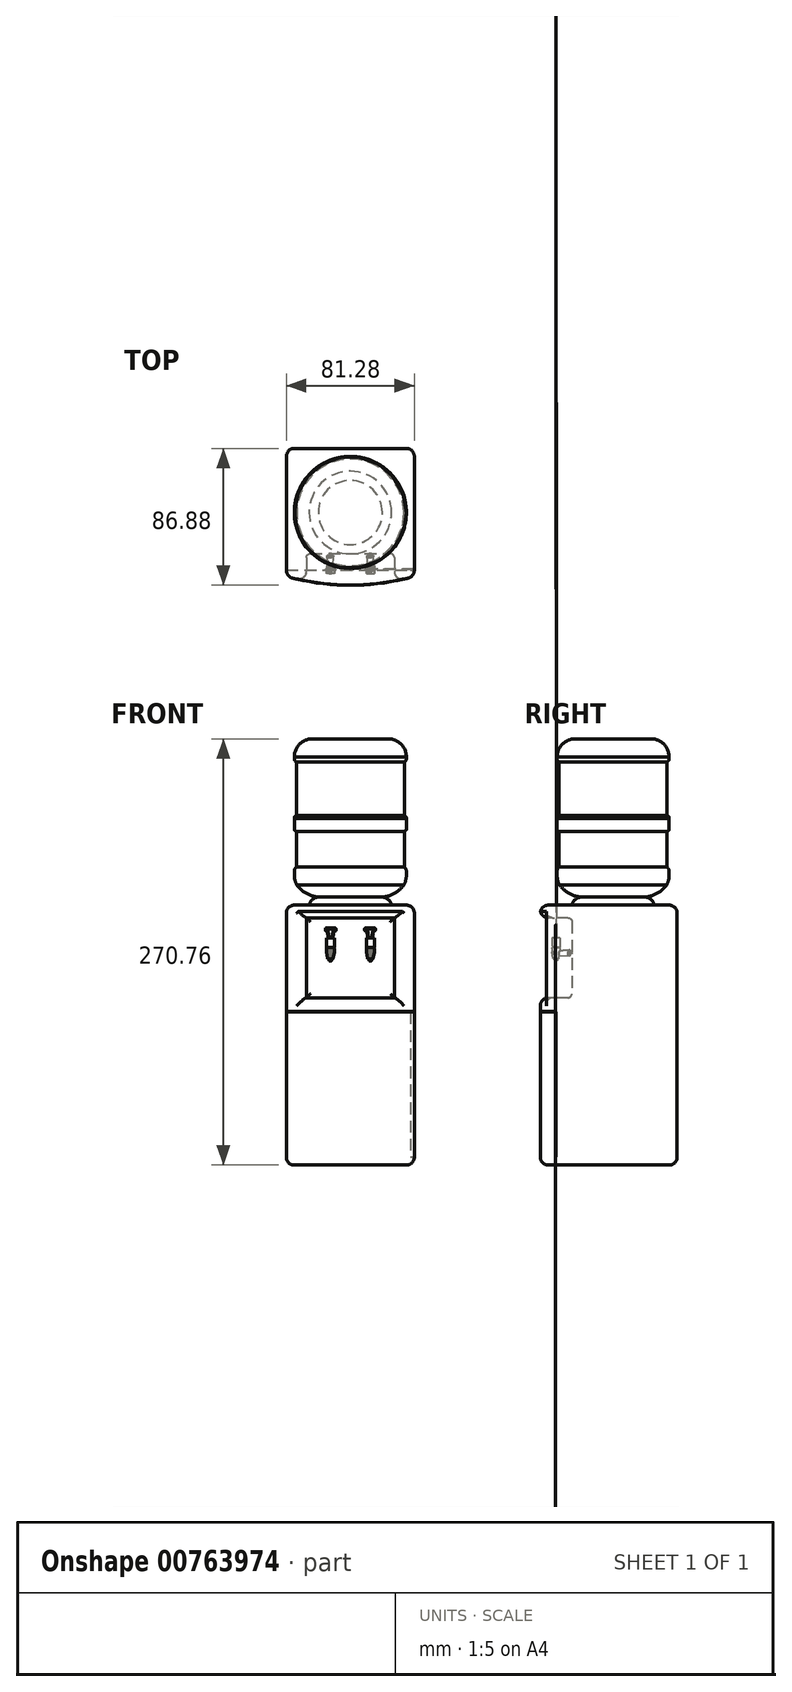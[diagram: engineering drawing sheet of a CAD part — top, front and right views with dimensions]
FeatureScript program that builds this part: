
annotation { "Feature Type Name" : "Feature", "Feature Type Description" : "" }
export const myFeature = defineFeature(function(context is Context, id is Id, definition is map)
    precondition{}
    {
        {
            var Q0;
            Q0=qCreatedBy(makeId("Front.planeOp"),FACE);
            var sketch = newSketch(context, id + "F0", { "sketchPlane" : qUnion([Q0])});
            skLineSegment(sketch, "E0", {"start": v(0, 95.92) * mm, "end": v(24.1, 95.92) * mm});
            skLineSegment(sketch, "E1", {"start": v(0, 11.85) * mm, "end": v(35.56, 11.85) * mm, "construction": true});
            skLineSegment(sketch, "E2", {"start": v(0, 83.22) * mm, "end": v(35.56, 83.22) * mm, "construction": true});
            skLineSegment(sketch, "E3", {"start": v(0, 81.19) * mm, "end": v(34.29, 81.11) * mm, "construction": true});
            skPoint(sketch, "E4.visualSharp", {"position": v(35.56, 95.92) * mm});
            skArc(sketch, "E4.filletArc", {"start": v(35.53, 84.46) * mm, "mid": v(32.2, 92.56) * mm, "end": v(24.1, 95.92) * mm});
            skLineSegment(sketch, "E5", {"start": v(35.53, 84.46) * mm, "end": v(35.56, 83.22) * mm});
            skLineSegment(sketch, "E6", {"start": v(0, 47.4) * mm, "end": v(38.08, 47.32) * mm, "construction": true});
            skLineSegment(sketch, "E7", {"start": v(34.29, 81.11) * mm, "end": v(34.29, 47.33) * mm});
            skLineSegment(sketch, "E8", {"start": v(0, 45.37) * mm, "end": v(35.56, 45.37) * mm, "construction": true});
            skLineSegment(sketch, "E9", {"start": v(0, 38.52) * mm, "end": v(35.56, 38.44) * mm, "construction": true});
            skLineSegment(sketch, "E10", {"start": v(0, 37.25) * mm, "end": v(34.29, 37.17) * mm, "construction": true});
            skArc(sketch, "E11", {"start": v(35.56, 83.22) * mm, "mid": v(35.23, 81.98) * mm, "end": v(34.29, 81.11) * mm});
            skArc(sketch, "E12", {"start": v(35.56, 45.37) * mm, "mid": v(35.23, 46.55) * mm, "end": v(34.29, 47.33) * mm});
            skArc(sketch, "E13", {"start": v(34.29, 37.17) * mm, "mid": v(35.19, 37.54) * mm, "end": v(35.56, 38.44) * mm});
            skLineSegment(sketch, "E14", {"start": v(35.56, 45.37) * mm, "end": v(35.56, 38.44) * mm});
            skLineSegment(sketch, "E15", {"start": v(0, 14.39) * mm, "end": v(34.3, 14.39) * mm, "construction": true});
            skLineSegment(sketch, "E16", {"start": v(0, 2.96) * mm, "end": v(33.95, 2.96) * mm, "construction": true});
            skLineSegment(sketch, "E17", {"start": v(34.29, 37.17) * mm, "end": v(34.3, 14.39) * mm});
            skLineSegment(sketch, "E18", {"start": v(0, -4.66) * mm, "end": v(20.35, -4.66) * mm, "construction": true});
            skLineSegment(sketch, "E19", {"start": v(0, -9.74) * mm, "end": v(26.2, -9.74) * mm});
            skArc(sketch, "E20", {"start": v(35.56, 11.85) * mm, "mid": v(35.22, 13.27) * mm, "end": v(34.3, 14.39) * mm});
            skLineSegment(sketch, "E21", {"start": v(35.56, 11.85) * mm, "end": v(35.57, 9.23) * mm});
            skArc(sketch, "E22", {"start": v(33.95, 2.96) * mm, "mid": v(35.16, 5.99) * mm, "end": v(35.57, 9.23) * mm});
            skArc(sketch, "E23", {"start": v(20.35, -4.66) * mm, "mid": v(27.95, -2.29) * mm, "end": v(33.95, 2.96) * mm});
            skArc(sketch, "E24", {"start": v(26.2, -9.74) * mm, "mid": v(24.13, -6.22) * mm, "end": v(20.35, -4.66) * mm});
            skLineSegment(sketch, "E25", {"start": v(0, 95.92) * mm, "end": v(0, -9.74) * mm});
            skSolve(sketch);
        }
        {
            var Q0;
            Q0 = qSketchRegion(id + "F0", true);
            var Q1;
            Q1=sQuery(id+"F0.wireOp",EDGE,"E25");
            revolve(context, id + "F1", {"surfaceOperationType" : NewSurfaceOperationType.NEW, "entities" : qUnion([Q0]), "axis" : qUnion([Q1]), "revolveType" : RevolveType.FULL});
        }
        {
            var Q0;
            Q0=makeQuery(id+"F1.opRevolve","SWEPT_FACE",FACE,{"disambiguationData":[OSD([sQuery(id+"F0.wireOp",EDGE,"E19")])]});
            cPlane(context, id + "F2", {"entities" : qUnion([Q0]), "cplaneType" : CPlaneType.OFFSET, "offset" : 0 * mm, "width" : 152.4 * mm, "height" : 152.4 * mm});
        }
        {
            var Q0;
            Q0=qCreatedBy(id+"F2.planeOp",FACE);
            var sketch = newSketch(context, id + "F3", { "sketchPlane" : qUnion([Q0])});
            skLineSegment(sketch, "E26.top", {"start": v(-40.64, -40.64) * mm, "end": v(40.64, -40.64) * mm});
            skLineSegment(sketch, "E26.left", {"start": v(-40.64, 40.64) * mm, "end": v(-40.64, -40.64) * mm});
            skLineSegment(sketch, "E26.right", {"start": v(40.64, 40.64) * mm, "end": v(40.64, -40.64) * mm});
            skArc(sketch, "E27", {"start": v(40.64, 40.64) * mm, "mid": v(0, 46.24) * mm, "end": v(-40.64, 40.64) * mm});
            skSolve(sketch);
        }
        {
            var Q0;
            Q0 = qSketchRegion(id + "F3", true);
            extrude(context, id + "F4", {"entities" : qUnion([Q0]), "operationType" : NewBodyOperationType.ADD, "depth" : 165.1 * mm, "offsetDistance" : 25.4 * mm});
        }
        {
            var Q0;
            Q0=qCreatedBy(makeId("Front.planeOp"),FACE);
            cPlane(context, id + "F5", {"entities" : qUnion([Q0]), "cplaneType" : CPlaneType.OFFSET, "offset" : 46.48 * mm, "width" : 152.4 * mm, "height" : 152.4 * mm});
        }
        {
            var Q0;
            Q0=qCreatedBy(id+"F5.planeOp",FACE);
            var sketch = newSketch(context, id + "F6", { "sketchPlane" : qUnion([Q0])});
            skLineSegment(sketch, "E28.bottom", {"start": v(-27.94, -17.78) * mm, "end": v(27.94, -17.78) * mm});
            skLineSegment(sketch, "E28.top", {"start": v(-27.94, -68.58) * mm, "end": v(27.94, -68.58) * mm});
            skLineSegment(sketch, "E28.left", {"start": v(-27.94, -17.78) * mm, "end": v(-27.94, -68.58) * mm});
            skLineSegment(sketch, "E28.right", {"start": v(27.94, -17.78) * mm, "end": v(27.94, -68.58) * mm});
            skSolve(sketch);
        }
        {
            var Q0;
            Q0 = qSketchRegion(id + "F6", true);
            extrude(context, id + "F7", {"entities" : qUnion([Q0]), "operationType" : NewBodyOperationType.REMOVE, "oppositeDirection" : true, "depth" : 20.32 * mm, "offsetDistance" : 25.4 * mm});
        }
        {
            var Q0;
            Q0=makeQuery(id+"F4.opExtrude","CAP_EDGE",EDGE,{"disambiguationData":[OSD([sQuery(id+"F3.wireOp",EDGE,"E26.left")])],"isStart":true});
            var Q1;
            Q1=makeQuery(id+"F4.opExtrude","SWEPT_EDGE",EDGE,{"disambiguationData":[OSD([sQuery(id+"F3.wireOp",EDGE,"E26.top"),sQuery(id+"F3.wireOp",EDGE,"E26.left")])]});
            var Q2;
            Q2=makeQuery(id+"F4.opExtrude","SWEPT_EDGE",EDGE,{"disambiguationData":[OSD([sQuery(id+"F3.wireOp",EDGE,"E26.left"),sQuery(id+"F3.wireOp",EDGE,"E27")])]});
            var Q3;
            Q3=makeQuery(id+"F4.opExtrude","CAP_EDGE",EDGE,{"disambiguationData":[OSD([sQuery(id+"F3.wireOp",EDGE,"E27")])],"isStart":true});
            var Q4;
            Q4=makeQuery(id+"F4.opExtrude","SWEPT_EDGE",EDGE,{"disambiguationData":[OSD([sQuery(id+"F3.wireOp",EDGE,"E26.right"),sQuery(id+"F3.wireOp",EDGE,"E27")])]});
            var Q5;
            Q5=makeQuery(id+"F4.opExtrude","CAP_EDGE",EDGE,{"disambiguationData":[OSD([sQuery(id+"F3.wireOp",EDGE,"E26.right")])],"isStart":true});
            var Q6;
            Q6=makeQuery(id+"F4.opExtrude","SWEPT_EDGE",EDGE,{"disambiguationData":[OSD([sQuery(id+"F3.wireOp",EDGE,"E26.top"),sQuery(id+"F3.wireOp",EDGE,"E26.right")])]});
            var Q7;
            Q7=makeQuery(id+"F4.opExtrude","CAP_EDGE",EDGE,{"disambiguationData":[OSD([sQuery(id+"F3.wireOp",EDGE,"E26.right")])],"isStart":false});
            var Q8;
            Q8=makeQuery(id+"F4.opExtrude","CAP_EDGE",EDGE,{"disambiguationData":[OSD([sQuery(id+"F3.wireOp",EDGE,"E27")])],"isStart":false});
            var Q9;
            Q9=makeQuery(id+"F4.opExtrude","CAP_EDGE",EDGE,{"disambiguationData":[OSD([sQuery(id+"F3.wireOp",EDGE,"E26.left")])],"isStart":false});
            var Q10;
            Q10=makeQuery(id+"F4.opExtrude","CAP_EDGE",EDGE,{"disambiguationData":[OSD([sQuery(id+"F3.wireOp",EDGE,"E26.top")])],"isStart":true});
            var Q11;
            Q11=makeQuery(id+"F4.opExtrude","CAP_EDGE",EDGE,{"disambiguationData":[OSD([sQuery(id+"F3.wireOp",EDGE,"E26.top")])],"isStart":false});
            fillet(context, id + "F8", {"entities" : qUnion([Q0, Q1, Q2, Q3, Q4, Q5, Q6, Q7, Q8, Q9, Q10, Q11]), "radius" : 5.08 * mm, "tangentPropagation" : true, "allowEdgeOverflow" : false});
        }
        {
            var Q0;
            Q0=qCreatedBy(id+"F5.planeOp",FACE);
            var sketch = newSketch(context, id + "F9", { "sketchPlane" : qUnion([Q0])});
            skLineSegment(sketch, "E29.bottom", {"start": v(-49.64, -77.18) * mm, "end": v(53.25, -77.18) * mm});
            skLineSegment(sketch, "E29.top", {"start": v(-49.64, -77.69) * mm, "end": v(53.25, -77.69) * mm});
            skLineSegment(sketch, "E29.left", {"start": v(-49.64, -77.18) * mm, "end": v(-49.64, -77.69) * mm});
            skLineSegment(sketch, "E29.right", {"start": v(53.25, -77.18) * mm, "end": v(53.25, -77.69) * mm});
            skSolve(sketch);
        }
        {
            var Q0;
            Q0 = qSketchRegion(id + "F9", true);
            extrude(context, id + "F10", {"entities" : qUnion([Q0]), "operationType" : NewBodyOperationType.REMOVE, "oppositeDirection" : true, "depth" : 9.9 * mm, "offsetDistance" : 25.4 * mm});
        }
        {
            var Q0;
            Q0=makeQuery(id+"F7.boolean.opBoolean","COPY",FACE,{"derivedFrom":makeQuery(id+"F7.opExtrude","CAP_FACE",FACE,{"disambiguationData":[OSD([sQuery(id+"F6.wireOp",EDGE,"E28.bottom"),sQuery(id+"F6.wireOp",EDGE,"E28.top"),sQuery(id+"F6.wireOp",EDGE,"E28.left"),sQuery(id+"F6.wireOp",EDGE,"E28.right")])],"isStart":false})});
            fillet(context, id + "F11", {"entities" : qUnion([Q0]), "radius" : 2.54 * mm, "tangentPropagation" : true, "allowEdgeOverflow" : false});
        }
        {
            var Q0;
            Q0=makeQuery(id+"F7.boolean.opBoolean","INTERSECT",EDGE,{"derivedFrom":[makeQuery(id+"F4.opExtrude","SWEPT_FACE",FACE,{"disambiguationData":[OSD([sQuery(id+"F3.wireOp",EDGE,"E27")])]}),makeQuery(id+"F7.opExtrude","SWEPT_FACE",FACE,{"disambiguationData":[OSD([sQuery(id+"F6.wireOp",EDGE,"E28.bottom")])]})]});
            var Q1;
            Q1=makeQuery(id+"F7.boolean.opBoolean","INTERSECT",EDGE,{"derivedFrom":[makeQuery(id+"F4.opExtrude","SWEPT_FACE",FACE,{"disambiguationData":[OSD([sQuery(id+"F3.wireOp",EDGE,"E27")])]}),makeQuery(id+"F7.opExtrude","SWEPT_FACE",FACE,{"disambiguationData":[OSD([sQuery(id+"F6.wireOp",EDGE,"E28.right")])]})]});
            var Q2;
            Q2=makeQuery(id+"F7.boolean.opBoolean","INTERSECT",EDGE,{"derivedFrom":[makeQuery(id+"F4.opExtrude","SWEPT_FACE",FACE,{"disambiguationData":[OSD([sQuery(id+"F3.wireOp",EDGE,"E27")])]}),makeQuery(id+"F7.opExtrude","SWEPT_FACE",FACE,{"disambiguationData":[OSD([sQuery(id+"F6.wireOp",EDGE,"E28.top")])]})]});
            var Q3;
            Q3=makeQuery(id+"F7.boolean.opBoolean","INTERSECT",EDGE,{"derivedFrom":[makeQuery(id+"F4.opExtrude","SWEPT_FACE",FACE,{"disambiguationData":[OSD([sQuery(id+"F3.wireOp",EDGE,"E27")])]}),makeQuery(id+"F7.opExtrude","SWEPT_FACE",FACE,{"disambiguationData":[OSD([sQuery(id+"F6.wireOp",EDGE,"E28.left")])]})]});
            fillet(context, id + "F12", {"entities" : qUnion([Q0, Q1, Q2, Q3]), "radius" : 5.08 * mm, "tangentPropagation" : true, "allowEdgeOverflow" : false});
        }
        {
            var Q0;
            Q0=makeQuery(id+"F4.opExtrude","SWEPT_FACE",FACE,{"disambiguationData":[OSD([sQuery(id+"F3.wireOp",EDGE,"E26.right")])]});
            var sketch = newSketch(context, id + "F13", { "sketchPlane" : qUnion([Q0])});
            skLineSegment(sketch, "E30.bottom", {"start": v(-36.23, -77.69) * mm, "end": v(-36.74, -77.69) * mm});
            skLineSegment(sketch, "E30.top", {"start": v(-36.23, -169.76) * mm, "end": v(-36.74, -169.76) * mm});
            skLineSegment(sketch, "E30.left", {"start": v(-36.23, -77.69) * mm, "end": v(-36.23, -169.76) * mm});
            skLineSegment(sketch, "E30.right", {"start": v(-36.74, -77.69) * mm, "end": v(-36.74, -169.76) * mm});
            skSolve(sketch);
        }
        {
            var Q0;
            Q0=makeQuery(id+"F13.imprint","IMPRINT",FACE,{"disambiguationData":[TD([[makeQuery(id+"F13.imprint","IMPRINT",EDGE,{"derivedFrom":sQuery(id+"F13.wireOp",EDGE,"E30.bottom")}),-1.0]])]});
            extrude(context, id + "F14", {"entities" : qUnion([Q0]), "operationType" : NewBodyOperationType.REMOVE, "oppositeDirection" : true, "depth" : 2.6 * mm, "offsetDistance" : 25.4 * mm});
        }
        {
            var Q0;
            Q0=qCreatedBy(makeId("Top.planeOp"),FACE);
            cPlane(context, id + "F15", {"entities" : qUnion([Q0]), "cplaneType" : CPlaneType.OFFSET, "offset" : 40.13 * mm, "oppositeDirection" : true, "width" : 152.4 * mm, "height" : 152.4 * mm});
        }
        {
            var Q0;
            Q0=qCreatedBy(id+"F15.planeOp",FACE);
            var sketch = newSketch(context, id + "F16", { "sketchPlane" : qUnion([Q0])});
            skLineSegment(sketch, "E31", {"start": v(-14.73, -26.16) * mm, "end": v(-14.22, -36.32) * mm});
            skLineSegment(sketch, "E32", {"start": v(-12.7, -26.16) * mm, "end": v(-12.7, -36.32) * mm});
            skLineSegment(sketch, "E33", {"start": v(-14.73, -26.16) * mm, "end": v(-12.7, -26.16) * mm});
            skLineSegment(sketch, "E34", {"start": v(-14.22, -36.32) * mm, "end": v(-12.7, -36.32) * mm});
            skSolve(sketch);
        }
        {
            var Q0;
            Q0=makeQuery(id+"F16.imprint","IMPRINT",FACE,{"disambiguationData":[TD([[makeQuery(id+"F16.imprint","IMPRINT",EDGE,{"derivedFrom":sQuery(id+"F16.wireOp",EDGE,"E31")}),1.0]])]});
            var Q1;
            Q1=sQuery(id+"F16.wireOp",EDGE,"E32");
            revolve(context, id + "F17", {"surfaceOperationType" : NewSurfaceOperationType.NEW, "entities" : qUnion([Q0]), "axis" : qUnion([Q1]), "revolveType" : RevolveType.FULL});
        }
        {
            var Q0;
            Q0=makeQuery(id+"F17.opRevolve","SWEPT_EDGE",EDGE,{"disambiguationData":[OSD([sQuery(id+"F16.wireOp",EDGE,"E31"),sQuery(id+"F16.wireOp",EDGE,"E33")])]});
            fillet(context, id + "F18", {"entities" : qUnion([Q0]), "radius" : 1.27 * mm, "tangentPropagation" : true, "allowEdgeOverflow" : false});
        }
        {
            var Q0;
            Q0=makeQuery(id+"F17.opRevolve","SWEPT_FACE",FACE,{"disambiguationData":[OSD([sQuery(id+"F16.wireOp",EDGE,"E34")])]});
            var sketch = newSketch(context, id + "F19", { "sketchPlane" : qUnion([Q0])});
            skLineSegment(sketch, "E35", {"start": v(-12.7, -40.13) * mm, "end": v(-12.7, -36.63) * mm});
            skLineSegment(sketch, "E36", {"start": v(-12.7, -36.63) * mm, "end": v(-10.72, -36.63) * mm});
            skLineSegment(sketch, "E37", {"start": v(-12.7, -40.13) * mm, "end": v(-12.7, -44) * mm});
            skLineSegment(sketch, "E38", {"start": v(-10.21, -37.11) * mm, "end": v(-10.1, -39.28) * mm});
            skLineSegment(sketch, "E39", {"start": v(-10.13, -39.53) * mm, "end": v(-10.94, -43.58) * mm});
            skLineSegment(sketch, "E40", {"start": v(-12.7, -44) * mm, "end": v(-12.7, -45.1) * mm});
            skLineSegment(sketch, "E41", {"start": v(-12.7, -45.1) * mm, "end": v(-12.1, -45.1) * mm});
            skLineSegment(sketch, "E42", {"start": v(-11.85, -44.85) * mm, "end": v(-11.85, -44.05) * mm});
            skLineSegment(sketch, "E43", {"start": v(-11.8, -44) * mm, "end": v(-11.44, -44) * mm});
            skPoint(sketch, "E44.visualSharp", {"position": v(-10.24, -36.63) * mm});
            skArc(sketch, "E44.filletArc", {"start": v(-10.21, -37.11) * mm, "mid": v(-10.37, -36.77) * mm, "end": v(-10.72, -36.63) * mm});
            skPoint(sketch, "E45.visualSharp", {"position": v(-10.1, -39.4) * mm});
            skArc(sketch, "E45.filletArc", {"start": v(-10.13, -39.53) * mm, "mid": v(-10.11, -39.4) * mm, "end": v(-10.1, -39.28) * mm});
            skPoint(sketch, "E46.visualSharp", {"position": v(-11.02, -44) * mm});
            skArc(sketch, "E46.filletArc", {"start": v(-11.44, -44) * mm, "mid": v(-11.12, -43.88) * mm, "end": v(-10.94, -43.58) * mm});
            skPoint(sketch, "E47.visualSharp", {"position": v(-11.85, -44) * mm});
            skArc(sketch, "E47.filletArc", {"start": v(-11.8, -44) * mm, "mid": v(-11.83, -44) * mm, "end": v(-11.85, -44.05) * mm});
            skPoint(sketch, "E48.visualSharp", {"position": v(-11.85, -45.1) * mm});
            skArc(sketch, "E48.filletArc", {"start": v(-12.1, -45.1) * mm, "mid": v(-11.92, -45.03) * mm, "end": v(-11.85, -44.85) * mm});
            skSolve(sketch);
        }
        {
            var Q0;
            {var subQ4=sQuery(id+"F19.wireOp",EDGE,"E36");Q0=makeQuery(id+"F19.imprint","IMPRINT",FACE,{"disambiguationData":[TD([[makeQuery(id+"F19.imprint","IMPRINT",EDGE,{"derivedFrom":subQ4}),-1.0]])]});}
            var Q1;
            Q1=sQuery(id+"F19.wireOp",EDGE,"E35");
            revolve(context, id + "F20", {"operationType" : NewBodyOperationType.ADD, "surfaceOperationType" : NewSurfaceOperationType.NEW, "entities" : qUnion([Q0]), "axis" : qUnion([Q1]), "revolveType" : RevolveType.FULL});
        }
        {
            var Q0;
            Q0=qCreatedBy(makeId("Right.planeOp"),FACE);
            cPlane(context, id + "F21", {"entities" : qUnion([Q0]), "cplaneType" : CPlaneType.OFFSET, "offset" : 12.7 * mm, "oppositeDirection" : true, "width" : 152.4 * mm, "height" : 152.4 * mm});
        }
        {
            var Q0;
            Q0=makeQuery(id+"F7.boolean.opBoolean","COPY",FACE,{"derivedFrom":makeQuery(id+"F7.opExtrude","CAP_FACE",FACE,{"disambiguationData":[OSD([sQuery(id+"F6.wireOp",EDGE,"E28.bottom"),sQuery(id+"F6.wireOp",EDGE,"E28.top"),sQuery(id+"F6.wireOp",EDGE,"E28.left"),sQuery(id+"F6.wireOp",EDGE,"E28.right")])],"isStart":false})});
            cPlane(context, id + "F22", {"entities" : qUnion([Q0]), "cplaneType" : CPlaneType.OFFSET, "offset" : 10.16 * mm, "width" : 152.4 * mm, "height" : 152.4 * mm});
        }
        {
            var Q0;
            Q0=qCreatedBy(id+"F21.planeOp",FACE);
            var sketch = newSketch(context, id + "F23", { "sketchPlane" : qUnion([Q0])});
            skLineSegment(sketch, "E49.bottom", {"start": v(-33.78, -30.63) * mm, "end": v(-38.86, -30.63) * mm});
            skLineSegment(sketch, "E49.top", {"start": v(-33.78, -36.63) * mm, "end": v(-36.83, -36.63) * mm});
            skLineSegment(sketch, "E49.left", {"start": v(-33.78, -30.63) * mm, "end": v(-33.78, -36.63) * mm});
            skLineSegment(sketch, "E49.right", {"start": v(-38.86, -30.63) * mm, "end": v(-38.86, -34.6) * mm});
            skPoint(sketch, "E50.visualSharp", {"position": v(-38.86, -36.63) * mm});
            skArc(sketch, "E50.filletArc", {"start": v(-38.86, -34.6) * mm, "mid": v(-38.27, -36.04) * mm, "end": v(-36.83, -36.63) * mm});
            skSolve(sketch);
        }
        {
            var Q0;
            Q0=makeQuery(id+"F23.imprint","IMPRINT",FACE,{"disambiguationData":[TD([[makeQuery(id+"F23.imprint","IMPRINT",EDGE,{"derivedFrom":sQuery(id+"F23.wireOp",EDGE,"E49.bottom")}),1.0]])]});
            extrude(context, id + "F24", {"entities" : qUnion([Q0]), "operationType" : NewBodyOperationType.ADD, "depth" : 2.54 * mm, "offsetDistance" : 25.4 * mm, "hasSecondDirection" : true, "secondDirectionOppositeDirection" : true, "secondDirectionDepth" : 2.54 * mm});
        }
        {
            var Q0;
            Q0=qCreatedBy(id+"F22.planeOp",FACE);
            var sketch = newSketch(context, id + "F25", { "sketchPlane" : qUnion([Q0])});
            skLineSegment(sketch, "E51.bottom", {"start": v(-15.34, -24.56) * mm, "end": v(-9.6, -24.56) * mm});
            skLineSegment(sketch, "E51.left", {"start": v(-15.6, -24.8) * mm, "end": v(-15.6, -25.78) * mm});
            skLineSegment(sketch, "E51.right", {"start": v(-9.34, -24.8) * mm, "end": v(-9.34, -25.74) * mm});
            skLineSegment(sketch, "E52", {"start": v(-14.5, -26.24) * mm, "end": v(-13.66, -30.63) * mm});
            skLineSegment(sketch, "E53", {"start": v(-11.3, -30.63) * mm, "end": v(-10.78, -26.22) * mm});
            skLineSegment(sketch, "E54", {"start": v(-15.34, -26.03) * mm, "end": v(-14.75, -26.03) * mm});
            skLineSegment(sketch, "E55", {"start": v(-10.53, -26) * mm, "end": v(-9.6, -26) * mm});
            skPoint(sketch, "E56.visualSharp", {"position": v(-10.75, -26) * mm});
            skArc(sketch, "E56.filletArc", {"start": v(-10.53, -26) * mm, "mid": v(-10.7, -26.06) * mm, "end": v(-10.78, -26.22) * mm});
            skPoint(sketch, "E57.visualSharp", {"position": v(-14.54, -26.03) * mm});
            skArc(sketch, "E57.filletArc", {"start": v(-14.5, -26.24) * mm, "mid": v(-14.58, -26.1) * mm, "end": v(-14.75, -26.03) * mm});
            skPoint(sketch, "E58.visualSharp", {"position": v(-15.6, -26.03) * mm});
            skArc(sketch, "E58.filletArc", {"start": v(-15.6, -25.78) * mm, "mid": v(-15.52, -25.96) * mm, "end": v(-15.34, -26.03) * mm});
            skPoint(sketch, "E59.visualSharp", {"position": v(-15.6, -24.56) * mm});
            skArc(sketch, "E59.filletArc", {"start": v(-15.34, -24.56) * mm, "mid": v(-15.52, -24.63) * mm, "end": v(-15.6, -24.8) * mm});
            skPoint(sketch, "E60.visualSharp", {"position": v(-9.34, -26) * mm});
            skArc(sketch, "E60.filletArc", {"start": v(-9.6, -26) * mm, "mid": v(-9.42, -25.92) * mm, "end": v(-9.34, -25.74) * mm});
            skPoint(sketch, "E61.visualSharp", {"position": v(-9.34, -24.56) * mm});
            skArc(sketch, "E61.filletArc", {"start": v(-9.34, -24.8) * mm, "mid": v(-9.42, -24.63) * mm, "end": v(-9.6, -24.56) * mm});
            skSolve(sketch);
        }
        {
            var Q0;
            Q0=makeQuery(id+"F24.opExtrude","SWEPT_FACE",FACE,{"disambiguationData":[OSD([sQuery(id+"F23.wireOp",EDGE,"E49.bottom")])]});
            cPlane(context, id + "F26", {"entities" : qUnion([Q0]), "cplaneType" : CPlaneType.OFFSET, "offset" : 0 * mm, "width" : 152.4 * mm, "height" : 152.4 * mm});
        }
        {
            var Q0;
            Q0=qCreatedBy(id+"F26.planeOp",FACE);
            var sketch = newSketch(context, id + "F27", { "sketchPlane" : qUnion([Q0])});
            skCircle(sketch, "E62", {"center": v(-13.67, -36.31) * mm, "radius": 0.25 * mm});
            skSolve(sketch);
        }
        {
            var Q0;
            Q0=makeQuery(id+"F27.imprint","IMPRINT",FACE,{"disambiguationData":[TD([[makeQuery(id+"F27.imprint","IMPRINT",EDGE,{"derivedFrom":sQuery(id+"F27.wireOp",EDGE,"E62")}),1.0]])]});
            var Q1;
            Q1 = qConstructionFilter(qBodyType(qCreatedBy(id + "F25" ,EDGE), BodyType.WIRE), ConstructionObject.NO);
            sweep(context, id + "F28", {"operationType" : NewBodyOperationType.ADD, "profiles" : qUnion([Q0]), "path" : qUnion([Q1])});
        }
        {
            var Q0;
            Q0=makeQuery(id+"F17.opRevolve","SWEPT_BODY",BODY,{"disambiguationData":[OSD([sQuery(id+"F16.wireOp",EDGE,"E31"),sQuery(id+"F16.wireOp",EDGE,"E32"),sQuery(id+"F16.wireOp",EDGE,"E33"),sQuery(id+"F16.wireOp",EDGE,"E34")])]});
            var Q1;
            Q1=qCreatedBy(makeId("Right.planeOp"),FACE);
            mirror(context, id + "F29", {"entities" : qUnion([Q0]), "mirrorPlane" : qUnion([Q1])});
        }
    });
